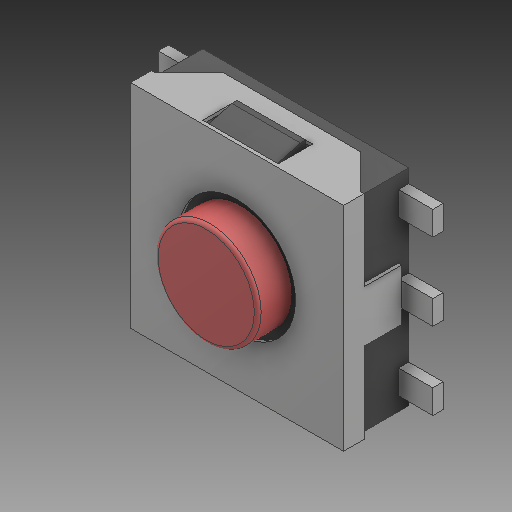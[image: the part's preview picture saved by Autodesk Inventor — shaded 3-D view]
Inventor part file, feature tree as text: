
AUTODESK INVENTOR PART (.ipt)
format: ipt  version: 2020 (Build 240168000, 168)  size: 179,712 bytes
history: native  units: mm
features: other x1, fillet x1
ambient origin geometry x8: Origin, YZ Plane, XZ Plane, XY Plane, X Axis, Y Axis, Z Axis, Center Point
bodies: Body1 (feature_tree)
feature tree (2):
  other  "Твердое тело1"
  fillet  "Fillet1"  [1 undecoded]
note: 1 required parameter value undecoded (feature->parameter linkage not recoverable at this tier; creation-order binding heuristic only, values carry confidence <= 0.55)
